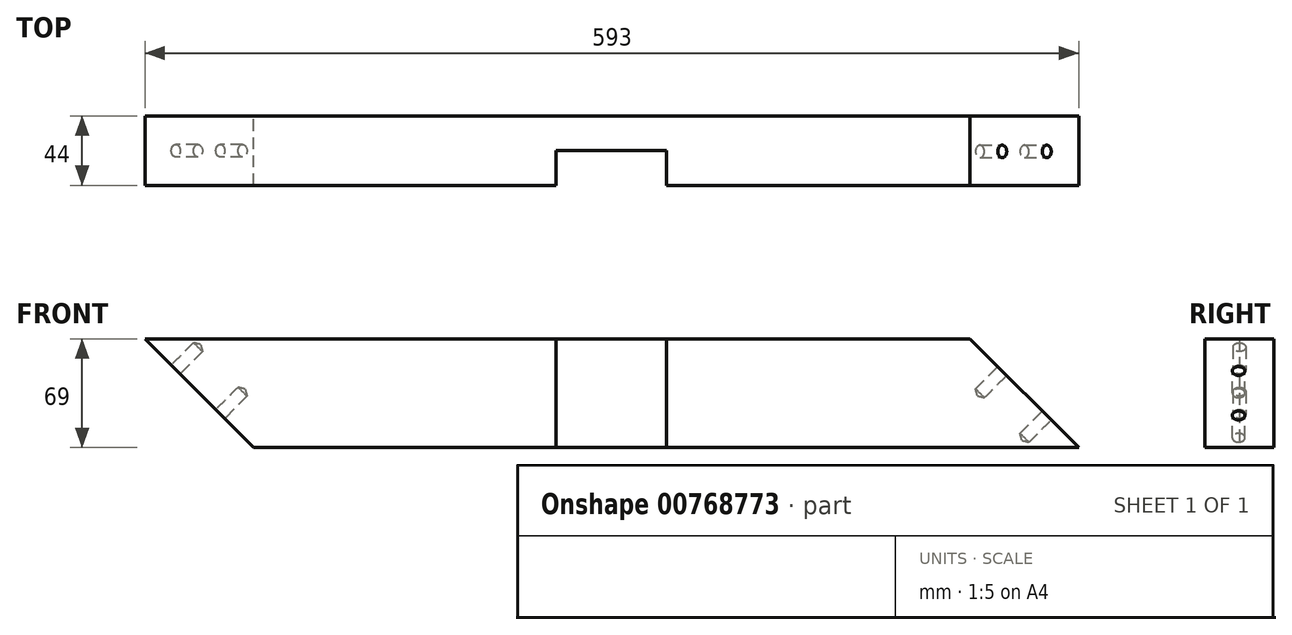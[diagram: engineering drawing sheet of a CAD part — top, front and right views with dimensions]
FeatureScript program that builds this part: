
annotation { "Feature Type Name" : "Feature", "Feature Type Description" : "" }
export const myFeature = defineFeature(function(context is Context, id is Id, definition is map)
    precondition{}
    {
        {
            var Q0;
            Q0=qCreatedBy(makeId("Right.planeOp"),FACE);
            var sketch = newSketch(context, id + "F0", { "sketchPlane" : qUnion([Q0])});
            skLineSegment(sketch, "E0.bottom", {"start": v(-19.66, 38.9) * mm, "end": v(24.34, 38.9) * mm});
            skLineSegment(sketch, "E0.top", {"start": v(-19.66, -30.1) * mm, "end": v(24.34, -30.1) * mm});
            skLineSegment(sketch, "E0.left", {"start": v(-19.66, 38.9) * mm, "end": v(-19.66, -30.1) * mm});
            skLineSegment(sketch, "E0.right", {"start": v(24.34, 38.9) * mm, "end": v(24.34, -30.1) * mm});
            skSolve(sketch);
        }
        {
            var Q0;
            Q0=makeQuery(id+"F0.imprint","IMPRINT",FACE,{"disambiguationData":[TD([[makeQuery(id+"F0.imprint","IMPRINT",EDGE,{"derivedFrom":sQuery(id+"F0.wireOp",EDGE,"E0.bottom")}),-1.0]])]});
            extrude(context, id + "F1", {"entities" : qUnion([Q0]), "depth" : (593) * mm, "offsetDistance" : 25 * mm});
        }
        {
            var Q0;
            Q0=makeQuery(id+"F1.opExtrude","CAP_EDGE",EDGE,{"disambiguationData":[OSD([sQuery(id+"F0.wireOp",EDGE,"E0.top")])],"isStart":true});
            chamfer(context, id + "F2", {"entities" : qUnion([Q0]), "width" : 69 * mm, "tangentPropagation" : true});
        }
        {
            var Q0;
            Q0=makeQuery(id+"F2.opChamfer","BLEND_FACE",FACE,{"disambiguationData":[OSD([sQuery(id+"F0.wireOp",EDGE,"E0.top")])]});
            var sketch = newSketch(context, id + "F3", { "sketchPlane" : qUnion([Q0])});
            skLineSegment(sketch, "E1", {"start": v(-2.34, 38.17) * mm, "end": v(-2.34, -77.76) * mm, "construction": true});
            skPoint(sketch, "E2", {"position": v(-2.34, 0) * mm});
            skPoint(sketch, "E3", {"position": v(-2.34, -40) * mm});
            skLineSegment(sketch, "E4", {"start": v(-35.7, -20) * mm, "end": v(34.97, -20) * mm, "construction": true});
            skSolve(sketch);
        }
        {
            var Q0;
            Q0=sQuery(id+"F3.wireOp",VERTEX,"E2");
            var Q1;
            Q1=sQuery(id+"F3.wireOp",VERTEX,"E3");
            var Q2;
            Q2=makeQuery(id+"F1.opExtrude","SWEPT_BODY",BODY,{"disambiguationData":[OSD([sQuery(id+"F0.wireOp",EDGE,"E0.bottom"),sQuery(id+"F0.wireOp",EDGE,"E0.top"),sQuery(id+"F0.wireOp",EDGE,"E0.left"),sQuery(id+"F0.wireOp",EDGE,"E0.right")])]});
            hole(context, id + "F4", {"style" : HoleStyle.SIMPLE, "endStyle" : HoleEndStyle.BLIND, "holeDiameter" : 8 * mm, "majorDiameter" : 5 * mm, "holeDepth" : 20 * mm, "isTappedThrough" : true, "tappedDepth" : 12 * mm, "tapClearance" : 3, "locations" : qUnion([Q0, Q1]), "scope" : qUnion([Q2])});
        }
        {
            var Q0;
            Q0=makeQuery(id+"F1.opExtrude","CAP_EDGE",EDGE,{"disambiguationData":[OSD([sQuery(id+"F0.wireOp",EDGE,"E0.bottom")])],"isStart":false});
            chamfer(context, id + "F5", {"entities" : qUnion([Q0]), "width" : 69 * mm, "tangentPropagation" : true});
        }
        {
            var Q0;
            Q0=makeQuery(id+"F5.opChamfer","BLEND_FACE",FACE,{"disambiguationData":[OSD([sQuery(id+"F0.wireOp",EDGE,"E0.bottom")])]});
            var sketch = newSketch(context, id + "F6", { "sketchPlane" : qUnion([Q0])});
            skLineSegment(sketch, "E5", {"start": v(1.85, -333.69) * mm, "end": v(1.85, -449.62) * mm, "construction": true});
            skPoint(sketch, "E6", {"position": v(1.85, -371.86) * mm});
            skPoint(sketch, "E7", {"position": v(1.85, -411.86) * mm});
            skLineSegment(sketch, "E8", {"start": v(-31.51, -391.86) * mm, "end": v(39.15, -391.86) * mm, "construction": true});
            skSolve(sketch);
        }
        {
            var Q0;
            Q0=sQuery(id+"F6.wireOp",VERTEX,"E6");
            var Q1;
            Q1=sQuery(id+"F6.wireOp",VERTEX,"E7");
            var Q2;
            Q2=makeQuery(id+"F1.opExtrude","SWEPT_BODY",BODY,{"disambiguationData":[OSD([sQuery(id+"F0.wireOp",EDGE,"E0.bottom"),sQuery(id+"F0.wireOp",EDGE,"E0.top"),sQuery(id+"F0.wireOp",EDGE,"E0.left"),sQuery(id+"F0.wireOp",EDGE,"E0.right")])]});
            hole(context, id + "F7", {"style" : HoleStyle.SIMPLE, "endStyle" : HoleEndStyle.BLIND, "holeDiameter" : 8 * mm, "majorDiameter" : 5 * mm, "holeDepth" : 20 * mm, "isTappedThrough" : true, "tappedDepth" : 12 * mm, "tapClearance" : 3, "locations" : qUnion([Q0, Q1]), "scope" : qUnion([Q2])});
        }
        {
            var Q0;
            Q0=makeQuery(id+"F1.opExtrude","SWEPT_FACE",FACE,{"disambiguationData":[OSD([sQuery(id+"F0.wireOp",EDGE,"E0.left")])]});
            var sketch = newSketch(context, id + "F8", { "sketchPlane" : qUnion([Q0])});
            skLineSegment(sketch, "E9", {"start": v(261, 38.9) * mm, "end": v(261, -30.1) * mm});
            skLineSegment(sketch, "E10", {"start": v(261, -30.1) * mm, "end": v(331, -30.1) * mm});
            skLineSegment(sketch, "E11", {"start": v(331, -30.1) * mm, "end": v(331, 38.9) * mm});
            skLineSegment(sketch, "E12", {"start": v(331, 38.9) * mm, "end": v(261, 38.9) * mm});
            skSolve(sketch);
        }
        {
            var Q0;
            Q0=makeQuery(id+"F8.imprint","IMPRINT",FACE,{"disambiguationData":[TD([[makeQuery(id+"F8.imprint","IMPRINT",EDGE,{"derivedFrom":sQuery(id+"F8.wireOp",EDGE,"E9")}),1.0]])]});
            extrude(context, id + "F9", {"entities" : qUnion([Q0]), "operationType" : NewBodyOperationType.REMOVE, "oppositeDirection" : true, "depth" : (44 / 2) * mm, "offsetDistance" : 25 * mm});
        }
    });
